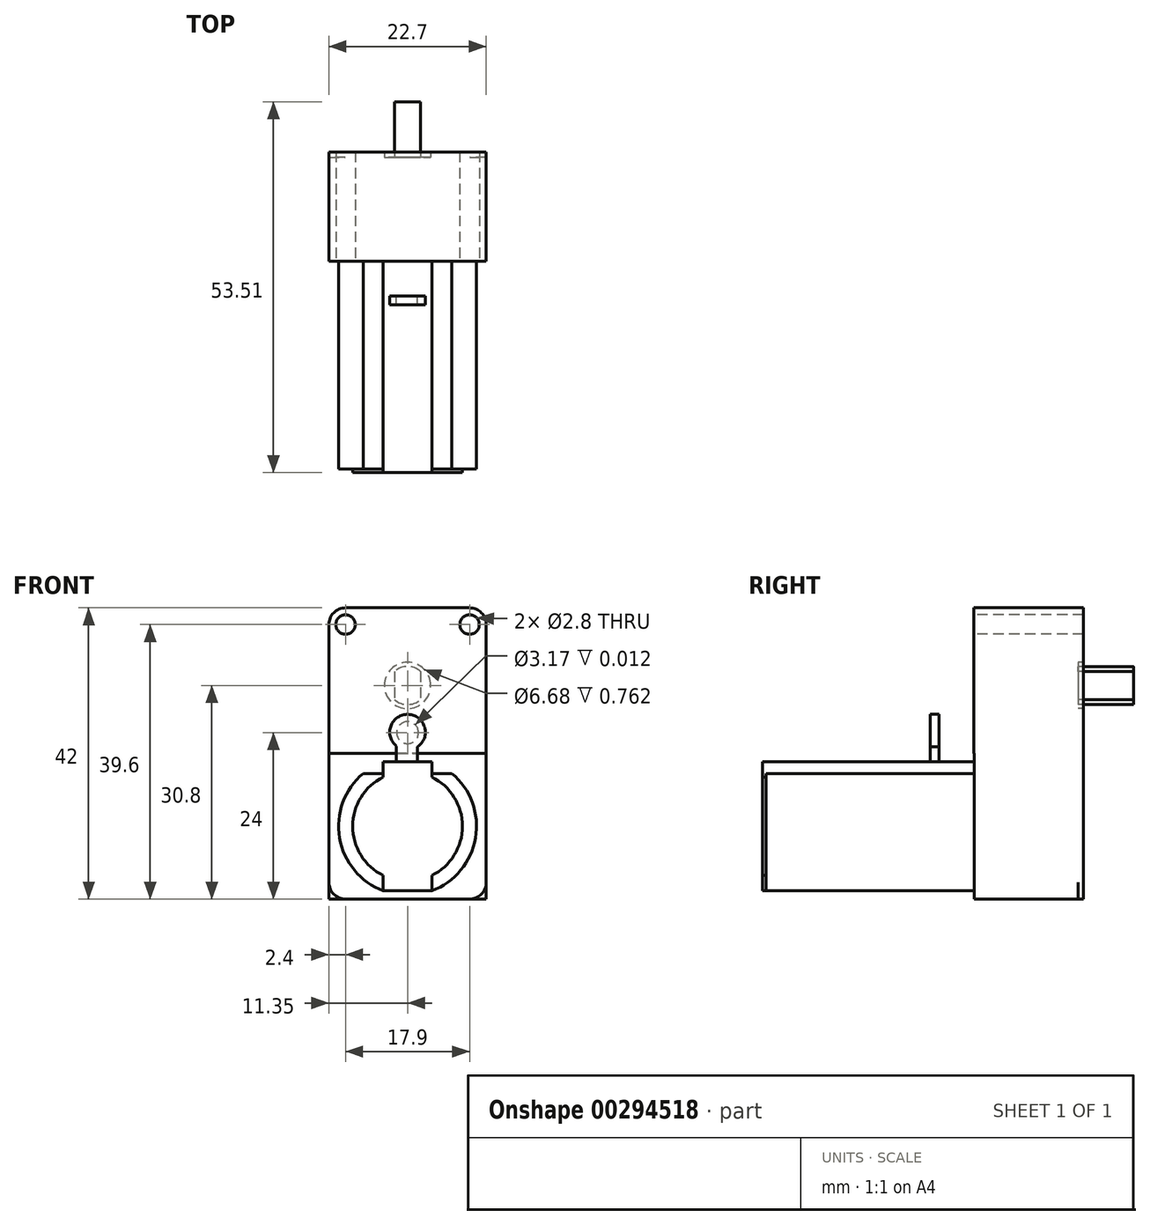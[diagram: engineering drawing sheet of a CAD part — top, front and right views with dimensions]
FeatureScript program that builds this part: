
annotation { "Feature Type Name" : "Feature", "Feature Type Description" : "" }
export const myFeature = defineFeature(function(context is Context, id is Id, definition is map)
    precondition{}
    {
        {
            var Q0;
            Q0=qCreatedBy(makeId("Top.planeOp"),FACE);
            var sketch = newSketch(context, id + "F0", { "sketchPlane" : qUnion([Q0])});
            skLineSegment(sketch, "E0.bottom", {"start": v(11.35, 22.5) * mm, "end": v(-11.35, 22.5) * mm});
            skLineSegment(sketch, "E0.top", {"start": v(11.35, -22.5) * mm, "end": v(-11.35, -22.5) * mm});
            skLineSegment(sketch, "E0.left", {"start": v(11.35, 22.5) * mm, "end": v(11.35, -22.5) * mm});
            skLineSegment(sketch, "E0.right", {"start": v(-11.35, 22.5) * mm, "end": v(-11.35, -22.5) * mm});
            skPoint(sketch, "E0.middle", {"position": v(0, 0) * mm});
            skLineSegment(sketch, "E1", {"start": v(-11.35, 7.5) * mm, "end": v(11.35, 7.5) * mm});
            skSolve(sketch);
        }
        {
            var Q0;
            {var subQ0=sQuery(id+"F0.wireOp",EDGE,"E0.bottom");Q0=makeQuery(id+"F0.imprint","IMPRINT",FACE,{"disambiguationData":[TD([[makeQuery(id+"F0.imprint","IMPRINT",EDGE,{"derivedFrom":subQ0}),1.0]])]});}
            extrude(context, id + "F1", {"entities" : qUnion([Q0]), "depth" : 42 * mm});
        }
        {
            var Q0;
            Q0 = qSketchRegion(id + "F0", true);
            extrude(context, id + "F2", {"entities" : qUnion([Q0]), "operationType" : NewBodyOperationType.ADD, "depth" : 21 * mm});
        }
        {
            var Q0;
            Q0=makeQuery(id+"F1.opExtrude","SWEPT_FACE",FACE,{"disambiguationData":[OSD([sQuery(id+"F0.wireOp",EDGE,"E1")])]});
            var sketch = newSketch(context, id + "F3", { "sketchPlane" : qUnion([Q0])});
            skLineSegment(sketch, "E2", {"start": v(0, 21) * mm, "end": v(0, 42) * mm});
            skCircle(sketch, "E3", {"center": v(0, 24) * mm, "radius": 1.59 * mm});
            skSolve(sketch);
        }
        {
            var Q0;
            {var subQ0=sQuery(id+"F3.wireOp",EDGE,"E3");var subQ1=sQuery(id+"F3.wireOp",EDGE,"E2");var subQ2=makeQuery(id+"F3.imprint","INTERSECT",VERTEX,{"disambiguationData":[OD(0.0)],"derivedFrom":[subQ1,subQ0]});Q0=makeQuery(id+"F3.imprint","IMPRINT",FACE,{"disambiguationData":[TD([[makeQuery(id+"F3.imprint","IMPRINT",EDGE,{"disambiguationData":[TD([[subQ2,-1.0]])],"derivedFrom":subQ1}),-1.0]])]});}
            var Q1;
            {var subQ0=sQuery(id+"F3.wireOp",EDGE,"E3");var subQ1=sQuery(id+"F3.wireOp",EDGE,"E2");var subQ2=makeQuery(id+"F3.imprint","INTERSECT",VERTEX,{"disambiguationData":[OD(0.0)],"derivedFrom":[subQ1,subQ0]});Q1=makeQuery(id+"F3.imprint","IMPRINT",FACE,{"disambiguationData":[TD([[makeQuery(id+"F3.imprint","IMPRINT",EDGE,{"disambiguationData":[TD([[subQ2,-1.0]])],"derivedFrom":subQ1}),1.0]])]});}
            extrude(context, id + "F4", {"entities" : qUnion([Q0, Q1]), "operationType" : NewBodyOperationType.ADD, "depth" : 5 / 406.4 * mm});
        }
        {
            var Q0;
            Q0=makeQuery(id+"F1.opExtrude","CAP_EDGE",EDGE,{"disambiguationData":[OSD([sQuery(id+"F0.wireOp",EDGE,"E0.right")])],"isStart":false});
            var Q1;
            Q1=makeQuery(id+"F1.opExtrude","CAP_EDGE",EDGE,{"disambiguationData":[OSD([sQuery(id+"F0.wireOp",EDGE,"E0.left")])],"isStart":false});
            fillet(context, id + "F5", {"entities" : qUnion([Q0, Q1]), "radius" : 2.4 * mm, "tangentPropagation" : true, "allowEdgeOverflow" : false});
        }
        {
            var Q0;
            Q0=makeQuery(id+"F1.opExtrude","SWEPT_FACE",FACE,{"disambiguationData":[OSD([sQuery(id+"F0.wireOp",EDGE,"E0.bottom")])]});
            var sketch = newSketch(context, id + "F6", { "sketchPlane" : qUnion([Q0])});
            skLineSegment(sketch, "E4", {"start": v(0, 42) * mm, "end": v(0, 0) * mm});
            skCircle(sketch, "E5", {"center": v(0, 30.8) * mm, "radius": 2.75 * mm});
            skLineSegment(sketch, "E6", {"start": v(-1.86, 32.83) * mm, "end": v(-1.86, 28.77) * mm});
            skLineSegment(sketch, "E7", {"start": v(1.86, 32.83) * mm, "end": v(1.86, 28.77) * mm});
            skCircle(sketch, "E8", {"center": v(0, 30.8) * mm, "radius": 3.34 * mm});
            skCircle(sketch, "E9", {"center": v(-8.95, 39.6) * mm, "radius": 1.4 * mm});
            skCircle(sketch, "E10", {"center": v(8.95, 39.6) * mm, "radius": 1.4 * mm});
            skSolve(sketch);
        }
        {
            var Q0;
            Q0=makeQuery(id+"F2.opExtrude","SWEPT_FACE",FACE,{"disambiguationData":[OSD([sQuery(id+"F0.wireOp",EDGE,"E0.top")])]});
            var sketch = newSketch(context, id + "F7", { "sketchPlane" : qUnion([Q0])});
            skLineSegment(sketch, "E11", {"start": v(0, 21) * mm, "end": v(0, 0) * mm});
            skLineSegment(sketch, "E12", {"start": v(-11.35, 10.5) * mm, "end": v(11.35, 10.5) * mm});
            skCircle(sketch, "E13", {"center": v(0, 10.5) * mm, "radius": 9.95 * mm});
            skLineSegment(sketch, "E14", {"start": v(-6.4, 18.12) * mm, "end": v(6.4, 18.12) * mm});
            skLineSegment(sketch, "E15", {"start": v(-6.4, 2.88) * mm, "end": v(6.4, 2.88) * mm});
            skLineSegment(sketch, "E16.bottom", {"start": v(11.35, 21) * mm, "end": v(-11.35, 21) * mm});
            skLineSegment(sketch, "E16.top", {"start": v(11.35, 0) * mm, "end": v(-11.35, 0) * mm});
            skLineSegment(sketch, "E16.left", {"start": v(11.35, 21) * mm, "end": v(11.35, 0) * mm});
            skLineSegment(sketch, "E16.right", {"start": v(-11.35, 21) * mm, "end": v(-11.35, 0) * mm});
            skLineSegment(sketch, "E17.bottom", {"start": v(3.5, 19.82) * mm, "end": v(-3.5, 19.82) * mm});
            skLineSegment(sketch, "E17.top", {"start": v(3.5, 1.18) * mm, "end": v(-3.5, 1.18) * mm});
            skLineSegment(sketch, "E17.left", {"start": v(3.5, 19.82) * mm, "end": v(3.5, 1.18) * mm});
            skLineSegment(sketch, "E17.right", {"start": v(-3.5, 19.82) * mm, "end": v(-3.5, 1.18) * mm});
            skCircle(sketch, "E18", {"center": v(0, 10.5) * mm, "radius": 7.92 * mm});
            skSolve(sketch);
        }
        {
            var Q0;
            {var subQ7=sQuery(id+"F7.wireOp",EDGE,"E16.bottom");var subQ8=sQuery(id+"F7.wireOp",EDGE,"E11");var subQ9=makeQuery(id+"F7.imprint","INTERSECT",VERTEX,{"derivedFrom":[subQ8,subQ7]});Q0=makeQuery(id+"F7.imprint","IMPRINT",FACE,{"disambiguationData":[TD([[makeQuery(id+"F7.imprint","IMPRINT",EDGE,{"disambiguationData":[TD([[subQ9,-1.0]])],"derivedFrom":subQ8}),1.0]])]});}
            var Q1;
            {var subQ2=sQuery(id+"F7.wireOp",EDGE,"E11");var subQ6=sQuery(id+"F7.wireOp",EDGE,"E16.bottom");var subQ11=makeQuery(id+"F7.imprint","INTERSECT",VERTEX,{"derivedFrom":[subQ2,subQ6]});Q1=makeQuery(id+"F7.imprint","IMPRINT",FACE,{"disambiguationData":[TD([[makeQuery(id+"F7.imprint","IMPRINT",EDGE,{"disambiguationData":[TD([[subQ11,-1.0]])],"derivedFrom":subQ2}),-1.0]])]});}
            var Q2;
            {var subQ0=sQuery(id+"F7.wireOp",EDGE,"E14");var subQ1=sQuery(id+"F7.wireOp",EDGE,"E13");var subQ2=makeQuery(id+"F7.imprint","INTERSECT",VERTEX,{"disambiguationData":[OD(1.0)],"derivedFrom":[subQ1,subQ0]});Q2=makeQuery(id+"F7.imprint","IMPRINT",FACE,{"disambiguationData":[TD([[makeQuery(id+"F7.imprint","IMPRINT",EDGE,{"disambiguationData":[TD([[subQ2,1.0]])],"derivedFrom":subQ0}),1.0]])]});}
            var Q3;
            {var subQ0=sQuery(id+"F7.wireOp",EDGE,"E14");var subQ1=sQuery(id+"F7.wireOp",EDGE,"E13");var subQ2=makeQuery(id+"F7.imprint","INTERSECT",VERTEX,{"disambiguationData":[OD(0.0)],"derivedFrom":[subQ1,subQ0]});Q3=makeQuery(id+"F7.imprint","IMPRINT",FACE,{"disambiguationData":[TD([[makeQuery(id+"F7.imprint","IMPRINT",EDGE,{"disambiguationData":[TD([[subQ2,-1.0]])],"derivedFrom":subQ0}),1.0]])]});}
            var Q4;
            {var subQ7=sQuery(id+"F7.wireOp",EDGE,"E16.top");var subQ9=sQuery(id+"F7.wireOp",EDGE,"E11");var subQ10=makeQuery(id+"F7.imprint","INTERSECT",VERTEX,{"derivedFrom":[subQ9,subQ7]});Q4=makeQuery(id+"F7.imprint","IMPRINT",FACE,{"disambiguationData":[TD([[makeQuery(id+"F7.imprint","IMPRINT",EDGE,{"disambiguationData":[TD([[subQ10,1.0]])],"derivedFrom":subQ9}),-1.0]])]});}
            var Q5;
            {var subQ7=sQuery(id+"F7.wireOp",EDGE,"E11");var subQ9=sQuery(id+"F7.wireOp",EDGE,"E16.top");var subQ10=makeQuery(id+"F7.imprint","INTERSECT",VERTEX,{"derivedFrom":[subQ7,subQ9]});Q5=makeQuery(id+"F7.imprint","IMPRINT",FACE,{"disambiguationData":[TD([[makeQuery(id+"F7.imprint","IMPRINT",EDGE,{"disambiguationData":[TD([[subQ10,1.0]])],"derivedFrom":subQ7}),1.0]])]});}
            var Q6;
            {var subQ0=sQuery(id+"F7.wireOp",EDGE,"E15");var subQ1=sQuery(id+"F7.wireOp",EDGE,"E13");var subQ2=makeQuery(id+"F7.imprint","INTERSECT",VERTEX,{"disambiguationData":[OD(1.0)],"derivedFrom":[subQ1,subQ0]});Q6=makeQuery(id+"F7.imprint","IMPRINT",FACE,{"disambiguationData":[TD([[makeQuery(id+"F7.imprint","IMPRINT",EDGE,{"disambiguationData":[TD([[subQ2,1.0]])],"derivedFrom":subQ0}),-1.0]])]});}
            var Q7;
            {var subQ0=sQuery(id+"F7.wireOp",EDGE,"E15");var subQ1=sQuery(id+"F7.wireOp",EDGE,"E13");var subQ2=makeQuery(id+"F7.imprint","INTERSECT",VERTEX,{"disambiguationData":[OD(0.0)],"derivedFrom":[subQ1,subQ0]});Q7=makeQuery(id+"F7.imprint","IMPRINT",FACE,{"disambiguationData":[TD([[makeQuery(id+"F7.imprint","IMPRINT",EDGE,{"disambiguationData":[TD([[subQ2,-1.0]])],"derivedFrom":subQ0}),-1.0]])]});}
            var Q8;
            {var subQ0=sQuery(id+"F7.wireOp",EDGE,"E13");var subQ1=sQuery(id+"F7.wireOp",EDGE,"E11");var subQ2=makeQuery(id+"F7.imprint","INTERSECT",VERTEX,{"disambiguationData":[OD(0.0)],"derivedFrom":[subQ1,subQ0]});Q8=makeQuery(id+"F7.imprint","IMPRINT",FACE,{"disambiguationData":[TD([[makeQuery(id+"F7.imprint","IMPRINT",EDGE,{"disambiguationData":[TD([[subQ2,-1.0]])],"derivedFrom":subQ1}),1.0]])]});}
            var Q9;
            {var subQ0=sQuery(id+"F7.wireOp",EDGE,"E13");var subQ1=sQuery(id+"F7.wireOp",EDGE,"E11");var subQ2=makeQuery(id+"F7.imprint","INTERSECT",VERTEX,{"disambiguationData":[OD(0.0)],"derivedFrom":[subQ1,subQ0]});Q9=makeQuery(id+"F7.imprint","IMPRINT",FACE,{"disambiguationData":[TD([[makeQuery(id+"F7.imprint","IMPRINT",EDGE,{"disambiguationData":[TD([[subQ2,-1.0]])],"derivedFrom":subQ1}),-1.0]])]});}
            var Q10;
            {var subQ0=sQuery(id+"F7.wireOp",EDGE,"E17.top");var subQ1=sQuery(id+"F7.wireOp",EDGE,"E11");var subQ2=makeQuery(id+"F7.imprint","INTERSECT",VERTEX,{"derivedFrom":[subQ1,subQ0]});Q10=makeQuery(id+"F7.imprint","IMPRINT",FACE,{"disambiguationData":[TD([[makeQuery(id+"F7.imprint","IMPRINT",EDGE,{"disambiguationData":[TD([[subQ2,-1.0]])],"derivedFrom":subQ1}),1.0]])]});}
            var Q11;
            {var subQ0=sQuery(id+"F7.wireOp",EDGE,"E17.top");var subQ1=sQuery(id+"F7.wireOp",EDGE,"E11");var subQ2=makeQuery(id+"F7.imprint","INTERSECT",VERTEX,{"derivedFrom":[subQ1,subQ0]});Q11=makeQuery(id+"F7.imprint","IMPRINT",FACE,{"disambiguationData":[TD([[makeQuery(id+"F7.imprint","IMPRINT",EDGE,{"disambiguationData":[TD([[subQ2,-1.0]])],"derivedFrom":subQ1}),-1.0]])]});}
            extrude(context, id + "F8", {"entities" : qUnion([Q0, Q1, Q2, Q3, Q4, Q5, Q6, Q7, Q8, Q9, Q10, Q11]), "operationType" : NewBodyOperationType.REMOVE, "oppositeDirection" : true, "depth" : 30 * mm});
        }
        {
            var Q0;
            Q0=makeQuery(id+"F1.opExtrude","SWEPT_FACE",FACE,{"disambiguationData":[OSD([sQuery(id+"F0.wireOp",EDGE,"E1")])]});
            cPlane(context, id + "F9", {"entities" : qUnion([Q0]), "cplaneType" : CPlaneType.OFFSET, "offset" : 5.04 * mm, "width" : 152.4 * mm, "height" : 152.4 * mm});
        }
        {
            var Q0;
            Q0=qCreatedBy(id+"F9.planeOp",FACE);
            var sketch = newSketch(context, id + "F10", { "sketchPlane" : qUnion([Q0])});
            skCircle(sketch, "E19", {"center": v(0, 24.07) * mm, "radius": 2.57 * mm});
            skLineSegment(sketch, "E20.bottom", {"start": v(-1.59, 23.8) * mm, "end": v(1.43, 23.8) * mm});
            skLineSegment(sketch, "E20.top", {"start": v(-1.59, 19.3) * mm, "end": v(1.43, 19.3) * mm});
            skLineSegment(sketch, "E20.left", {"start": v(-1.59, 23.8) * mm, "end": v(-1.59, 19.3) * mm});
            skLineSegment(sketch, "E20.right", {"start": v(1.43, 23.8) * mm, "end": v(1.43, 19.3) * mm});
            skSolve(sketch);
        }
        {
            var Q0;
            Q0 = qSketchRegion(id + "F10", true);
            extrude(context, id + "F11", {"entities" : qUnion([Q0]), "operationType" : NewBodyOperationType.ADD, "depth" : 1.27 * mm});
        }
        {
            var Q0;
            {var subQ0=sQuery(id+"F0.wireOp",EDGE,"E0.left");Q0=makeQuery(id+"F2.boolean.opBoolean","MERGE",EDGE,{"derivedFrom":[makeQuery(id+"F1.opExtrude","CAP_EDGE",EDGE,{"disambiguationData":[OSD([subQ0])],"isStart":true}),makeQuery(id+"F2.opExtrude","CAP_EDGE",EDGE,{"disambiguationData":[OSD([subQ0])],"isStart":true})]});}
            var Q1;
            {var subQ0=sQuery(id+"F0.wireOp",EDGE,"E0.right");Q1=makeQuery(id+"F2.boolean.opBoolean","MERGE",EDGE,{"derivedFrom":[makeQuery(id+"F1.opExtrude","CAP_EDGE",EDGE,{"disambiguationData":[OSD([subQ0])],"isStart":true}),makeQuery(id+"F2.opExtrude","CAP_EDGE",EDGE,{"disambiguationData":[OSD([subQ0])],"isStart":true})]});}
            fillet(context, id + "F12", {"entities" : qUnion([Q0, Q1]), "radius" : 2.4 * mm, "tangentPropagation" : true, "allowEdgeOverflow" : false});
        }
        {
            var Q0;
            {var subQ4=sQuery(id+"F6.wireOp",EDGE,"E7");Q0=makeQuery(id+"F6.imprint","IMPRINT",FACE,{"disambiguationData":[TD([[makeQuery(id+"F6.imprint","IMPRINT",EDGE,{"derivedFrom":subQ4}),-1.0]])]});}
            var Q1;
            {var subQ4=sQuery(id+"F6.wireOp",EDGE,"E6");Q1=makeQuery(id+"F6.imprint","IMPRINT",FACE,{"disambiguationData":[TD([[makeQuery(id+"F6.imprint","IMPRINT",EDGE,{"derivedFrom":subQ4}),1.0]])]});}
            extrude(context, id + "F13", {"entities" : qUnion([Q0, Q1]), "operationType" : NewBodyOperationType.ADD, "depth" : 8 * mm});
        }
        {
            var Q0;
            {var subQ3=sQuery(id+"F6.wireOp",EDGE,"E4");var subQ7=sQuery(id+"F6.wireOp",EDGE,"E8");var subQ9=makeQuery(id+"F6.imprint","INTERSECT",VERTEX,{"disambiguationData":[OD(0.0)],"derivedFrom":[subQ3,subQ7]});Q0=makeQuery(id+"F6.imprint","IMPRINT",FACE,{"disambiguationData":[TD([[makeQuery(id+"F6.imprint","IMPRINT",EDGE,{"disambiguationData":[TD([[subQ9,-1.0]])],"derivedFrom":subQ3}),1.0]])]});}
            var Q1;
            {var subQ4=sQuery(id+"F6.wireOp",EDGE,"E4");var subQ6=sQuery(id+"F6.wireOp",EDGE,"E8");var subQ9=makeQuery(id+"F6.imprint","INTERSECT",VERTEX,{"disambiguationData":[OD(0.0)],"derivedFrom":[subQ4,subQ6]});Q1=makeQuery(id+"F6.imprint","IMPRINT",FACE,{"disambiguationData":[TD([[makeQuery(id+"F6.imprint","IMPRINT",EDGE,{"disambiguationData":[TD([[subQ9,-1.0]])],"derivedFrom":subQ4}),-1.0]])]});}
            extrude(context, id + "F14", {"entities" : qUnion([Q0, Q1]), "operationType" : NewBodyOperationType.ADD, "depth" : 0.76 * mm});
        }
        {
            var Q0;
            Q0=makeQuery(id+"F6.imprint","IMPRINT",FACE,{"disambiguationData":[TD([[makeQuery(id+"F6.imprint","IMPRINT",EDGE,{"derivedFrom":sQuery(id+"F6.wireOp",EDGE,"E9")}),1.0]])]});
            var Q1;
            Q1=makeQuery(id+"F6.imprint","IMPRINT",FACE,{"disambiguationData":[TD([[makeQuery(id+"F6.imprint","IMPRINT",EDGE,{"derivedFrom":sQuery(id+"F6.wireOp",EDGE,"E10")}),1.0]])]});
            extrude(context, id + "F15", {"entities" : qUnion([Q0, Q1]), "operationType" : NewBodyOperationType.REMOVE, "oppositeDirection" : true, "depth" : 25.4 * mm});
        }
        {
            var Q0;
            {var subQ0=sQuery(id+"F7.wireOp",EDGE,"E17.left");var subQ1=sQuery(id+"F7.wireOp",EDGE,"E12");var subQ2=makeQuery(id+"F7.imprint","INTERSECT",VERTEX,{"derivedFrom":[subQ1,subQ0]});Q0=makeQuery(id+"F7.imprint","IMPRINT",FACE,{"disambiguationData":[TD([[makeQuery(id+"F7.imprint","IMPRINT",EDGE,{"disambiguationData":[TD([[subQ2,-1.0]])],"derivedFrom":subQ1}),1.0]])]});}
            var Q1;
            {var subQ5=sQuery(id+"F7.wireOp",EDGE,"E14");var subQ7=sQuery(id+"F7.wireOp",EDGE,"E11");var subQ8=makeQuery(id+"F7.imprint","INTERSECT",VERTEX,{"derivedFrom":[subQ7,subQ5]});Q1=makeQuery(id+"F7.imprint","IMPRINT",FACE,{"disambiguationData":[TD([[makeQuery(id+"F7.imprint","IMPRINT",EDGE,{"disambiguationData":[TD([[subQ8,-1.0]])],"derivedFrom":subQ7}),1.0]])]});}
            var Q2;
            {var subQ5=sQuery(id+"F7.wireOp",EDGE,"E14");var subQ6=sQuery(id+"F7.wireOp",EDGE,"E11");var subQ7=makeQuery(id+"F7.imprint","INTERSECT",VERTEX,{"derivedFrom":[subQ6,subQ5]});Q2=makeQuery(id+"F7.imprint","IMPRINT",FACE,{"disambiguationData":[TD([[makeQuery(id+"F7.imprint","IMPRINT",EDGE,{"disambiguationData":[TD([[subQ7,-1.0]])],"derivedFrom":subQ6}),-1.0]])]});}
            var Q3;
            {var subQ0=sQuery(id+"F7.wireOp",EDGE,"E18");var subQ1=sQuery(id+"F7.wireOp",EDGE,"E12");var subQ2=makeQuery(id+"F7.imprint","INTERSECT",VERTEX,{"disambiguationData":[OD(0.0)],"derivedFrom":[subQ1,subQ0]});Q3=makeQuery(id+"F7.imprint","IMPRINT",FACE,{"disambiguationData":[TD([[makeQuery(id+"F7.imprint","IMPRINT",EDGE,{"disambiguationData":[TD([[subQ2,-1.0]])],"derivedFrom":subQ1}),1.0]])]});}
            var Q4;
            {var subQ0=sQuery(id+"F7.wireOp",EDGE,"E18");var subQ1=sQuery(id+"F7.wireOp",EDGE,"E12");var subQ2=makeQuery(id+"F7.imprint","INTERSECT",VERTEX,{"disambiguationData":[OD(0.0)],"derivedFrom":[subQ1,subQ0]});Q4=makeQuery(id+"F7.imprint","IMPRINT",FACE,{"disambiguationData":[TD([[makeQuery(id+"F7.imprint","IMPRINT",EDGE,{"disambiguationData":[TD([[subQ2,-1.0]])],"derivedFrom":subQ1}),-1.0]])]});}
            var Q5;
            {var subQ1=sQuery(id+"F7.wireOp",EDGE,"E12");var subQ6=sQuery(id+"F7.wireOp",EDGE,"E11");var subQ9=makeQuery(id+"F7.imprint","INTERSECT",VERTEX,{"derivedFrom":[subQ6,subQ1]});Q5=makeQuery(id+"F7.imprint","IMPRINT",FACE,{"disambiguationData":[TD([[makeQuery(id+"F7.imprint","IMPRINT",EDGE,{"disambiguationData":[TD([[subQ9,-1.0]])],"derivedFrom":subQ6}),-1.0]])]});}
            var Q6;
            {var subQ1=sQuery(id+"F7.wireOp",EDGE,"E12");var subQ6=sQuery(id+"F7.wireOp",EDGE,"E11");var subQ9=makeQuery(id+"F7.imprint","INTERSECT",VERTEX,{"derivedFrom":[subQ6,subQ1]});Q6=makeQuery(id+"F7.imprint","IMPRINT",FACE,{"disambiguationData":[TD([[makeQuery(id+"F7.imprint","IMPRINT",EDGE,{"disambiguationData":[TD([[subQ9,-1.0]])],"derivedFrom":subQ6}),1.0]])]});}
            var Q7;
            {var subQ0=sQuery(id+"F7.wireOp",EDGE,"E17.left");var subQ1=sQuery(id+"F7.wireOp",EDGE,"E12");var subQ2=makeQuery(id+"F7.imprint","INTERSECT",VERTEX,{"derivedFrom":[subQ1,subQ0]});Q7=makeQuery(id+"F7.imprint","IMPRINT",FACE,{"disambiguationData":[TD([[makeQuery(id+"F7.imprint","IMPRINT",EDGE,{"disambiguationData":[TD([[subQ2,-1.0]])],"derivedFrom":subQ1}),-1.0]])]});}
            var Q8;
            {var subQ0=sQuery(id+"F7.wireOp",EDGE,"E18");var subQ1=sQuery(id+"F7.wireOp",EDGE,"E11");var subQ2=makeQuery(id+"F7.imprint","INTERSECT",VERTEX,{"disambiguationData":[OD(0.0)],"derivedFrom":[subQ1,subQ0]});Q8=makeQuery(id+"F7.imprint","IMPRINT",FACE,{"disambiguationData":[TD([[makeQuery(id+"F7.imprint","IMPRINT",EDGE,{"disambiguationData":[TD([[subQ2,-1.0]])],"derivedFrom":subQ1}),1.0]])]});}
            var Q9;
            {var subQ0=sQuery(id+"F7.wireOp",EDGE,"E18");var subQ1=sQuery(id+"F7.wireOp",EDGE,"E11");var subQ2=makeQuery(id+"F7.imprint","INTERSECT",VERTEX,{"disambiguationData":[OD(0.0)],"derivedFrom":[subQ1,subQ0]});Q9=makeQuery(id+"F7.imprint","IMPRINT",FACE,{"disambiguationData":[TD([[makeQuery(id+"F7.imprint","IMPRINT",EDGE,{"disambiguationData":[TD([[subQ2,-1.0]])],"derivedFrom":subQ1}),-1.0]])]});}
            var Q10;
            {var subQ0=sQuery(id+"F7.wireOp",EDGE,"E15");var subQ1=sQuery(id+"F7.wireOp",EDGE,"E11");var subQ2=makeQuery(id+"F7.imprint","INTERSECT",VERTEX,{"derivedFrom":[subQ1,subQ0]});Q10=makeQuery(id+"F7.imprint","IMPRINT",FACE,{"disambiguationData":[TD([[makeQuery(id+"F7.imprint","IMPRINT",EDGE,{"disambiguationData":[TD([[subQ2,-1.0]])],"derivedFrom":subQ1}),1.0]])]});}
            var Q11;
            {var subQ0=sQuery(id+"F7.wireOp",EDGE,"E15");var subQ1=sQuery(id+"F7.wireOp",EDGE,"E11");var subQ2=makeQuery(id+"F7.imprint","INTERSECT",VERTEX,{"derivedFrom":[subQ1,subQ0]});Q11=makeQuery(id+"F7.imprint","IMPRINT",FACE,{"disambiguationData":[TD([[makeQuery(id+"F7.imprint","IMPRINT",EDGE,{"disambiguationData":[TD([[subQ2,-1.0]])],"derivedFrom":subQ1}),-1.0]])]});}
            var Q12;
            {var subQ1=sQuery(id+"F7.wireOp",EDGE,"E17.bottom");var subQ3=sQuery(id+"F7.wireOp",EDGE,"E11");var subQ4=makeQuery(id+"F7.imprint","INTERSECT",VERTEX,{"derivedFrom":[subQ3,subQ1]});Q12=makeQuery(id+"F7.imprint","IMPRINT",FACE,{"disambiguationData":[TD([[makeQuery(id+"F7.imprint","IMPRINT",EDGE,{"disambiguationData":[TD([[subQ4,-1.0]])],"derivedFrom":subQ3}),1.0]])]});}
            var Q13;
            {var subQ1=sQuery(id+"F7.wireOp",EDGE,"E17.bottom");var subQ5=sQuery(id+"F7.wireOp",EDGE,"E11");var subQ6=makeQuery(id+"F7.imprint","INTERSECT",VERTEX,{"derivedFrom":[subQ5,subQ1]});Q13=makeQuery(id+"F7.imprint","IMPRINT",FACE,{"disambiguationData":[TD([[makeQuery(id+"F7.imprint","IMPRINT",EDGE,{"disambiguationData":[TD([[subQ6,-1.0]])],"derivedFrom":subQ5}),-1.0]])]});}
            var Q14;
            {var subQ0=sQuery(id+"F7.wireOp",EDGE,"E17.right");var subQ1=sQuery(id+"F7.wireOp",EDGE,"E14");var subQ2=makeQuery(id+"F7.imprint","INTERSECT",VERTEX,{"derivedFrom":[subQ1,subQ0]});Q14=makeQuery(id+"F7.imprint","IMPRINT",FACE,{"disambiguationData":[TD([[makeQuery(id+"F7.imprint","IMPRINT",EDGE,{"disambiguationData":[TD([[subQ2,-1.0]])],"derivedFrom":subQ1}),-1.0]])]});}
            var Q15;
            {var subQ0=sQuery(id+"F7.wireOp",EDGE,"E18");var subQ1=sQuery(id+"F7.wireOp",EDGE,"E14");var subQ2=makeQuery(id+"F7.imprint","INTERSECT",VERTEX,{"disambiguationData":[OD(1.0)],"derivedFrom":[subQ1,subQ0]});Q15=makeQuery(id+"F7.imprint","IMPRINT",FACE,{"disambiguationData":[TD([[makeQuery(id+"F7.imprint","IMPRINT",EDGE,{"disambiguationData":[TD([[subQ2,-1.0]])],"derivedFrom":subQ1}),-1.0]])]});}
            var Q16;
            {var subQ5=sQuery(id+"F7.wireOp",EDGE,"E18");var subQ7=sQuery(id+"F7.wireOp",EDGE,"E11");var subQ8=makeQuery(id+"F7.imprint","INTERSECT",VERTEX,{"disambiguationData":[OD(1.0)],"derivedFrom":[subQ7,subQ5]});Q16=makeQuery(id+"F7.imprint","IMPRINT",FACE,{"disambiguationData":[TD([[makeQuery(id+"F7.imprint","IMPRINT",EDGE,{"disambiguationData":[TD([[subQ8,-1.0]])],"derivedFrom":subQ7}),1.0]])]});}
            var Q17;
            {var subQ5=sQuery(id+"F7.wireOp",EDGE,"E11");var subQ7=sQuery(id+"F7.wireOp",EDGE,"E18");var subQ9=makeQuery(id+"F7.imprint","INTERSECT",VERTEX,{"disambiguationData":[OD(1.0)],"derivedFrom":[subQ5,subQ7]});Q17=makeQuery(id+"F7.imprint","IMPRINT",FACE,{"disambiguationData":[TD([[makeQuery(id+"F7.imprint","IMPRINT",EDGE,{"disambiguationData":[TD([[subQ9,-1.0]])],"derivedFrom":subQ5}),-1.0]])]});}
            var Q18;
            {var subQ0=sQuery(id+"F7.wireOp",EDGE,"E17.right");var subQ1=sQuery(id+"F7.wireOp",EDGE,"E15");var subQ2=makeQuery(id+"F7.imprint","INTERSECT",VERTEX,{"derivedFrom":[subQ1,subQ0]});Q18=makeQuery(id+"F7.imprint","IMPRINT",FACE,{"disambiguationData":[TD([[makeQuery(id+"F7.imprint","IMPRINT",EDGE,{"disambiguationData":[TD([[subQ2,-1.0]])],"derivedFrom":subQ1}),1.0]])]});}
            var Q19;
            {var subQ0=sQuery(id+"F7.wireOp",EDGE,"E18");var subQ1=sQuery(id+"F7.wireOp",EDGE,"E15");var subQ2=makeQuery(id+"F7.imprint","INTERSECT",VERTEX,{"disambiguationData":[OD(1.0)],"derivedFrom":[subQ1,subQ0]});Q19=makeQuery(id+"F7.imprint","IMPRINT",FACE,{"disambiguationData":[TD([[makeQuery(id+"F7.imprint","IMPRINT",EDGE,{"disambiguationData":[TD([[subQ2,-1.0]])],"derivedFrom":subQ1}),1.0]])]});}
            extrude(context, id + "F16", {"entities" : qUnion([Q0, Q1, Q2, Q3, Q4, Q5, Q6, Q7, Q8, Q9, Q10, Q11, Q12, Q13, Q14, Q15, Q16, Q17, Q18, Q19]), "operationType" : NewBodyOperationType.ADD, "depth" : 0.5 * mm});
        }
    });
